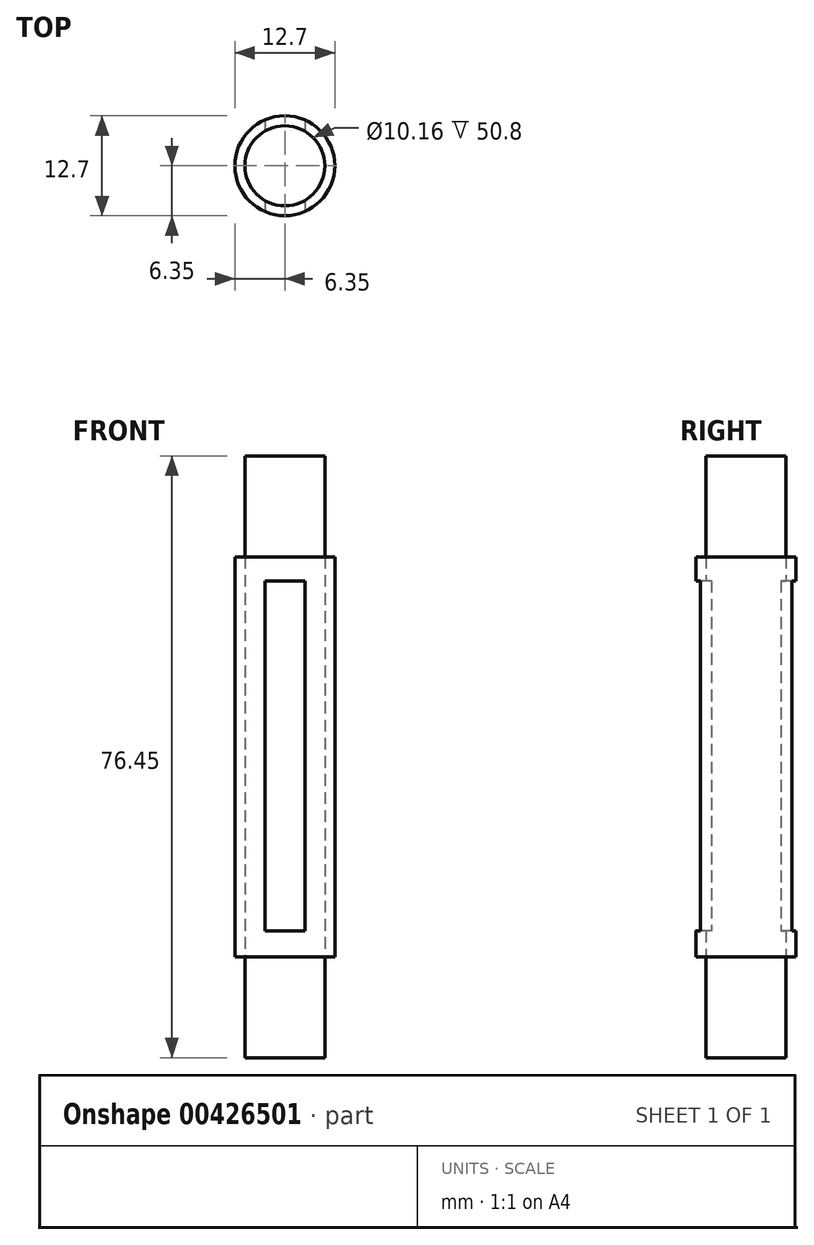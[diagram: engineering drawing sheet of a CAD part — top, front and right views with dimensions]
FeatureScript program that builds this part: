
annotation { "Feature Type Name" : "Feature", "Feature Type Description" : "" }
export const myFeature = defineFeature(function(context is Context, id is Id, definition is map)
    precondition{}
    {
        {
            var Q0;
            Q0=qCreatedBy(makeId("Top.planeOp"),FACE);
            var sketch = newSketch(context, id + "F0", { "sketchPlane" : qUnion([Q0])});
            skCircle(sketch, "E0", {"center": v(0, 0) * mm, "radius": 5.08 * mm});
            skSolve(sketch);
        }
        {
            var Q0;
            Q0=makeQuery(id+"F0.imprint","IMPRINT",FACE,{"disambiguationData":[TD([[makeQuery(id+"F0.imprint","IMPRINT",EDGE,{"derivedFrom":sQuery(id+"F0.wireOp",EDGE,"E0")}),1.0]])]});
            extrude(context, id + "F1", {"entities" : qUnion([Q0]), "depth" : 12.83 * mm});
        }
        {
            var Q0;
            Q0=makeQuery(id+"F1.opExtrude","CAP_FACE",FACE,{"disambiguationData":[OSD([sQuery(id+"F0.wireOp",EDGE,"E0")])],"isStart":false});
            var sketch = newSketch(context, id + "F2", { "sketchPlane" : qUnion([Q0])});
            skCircle(sketch, "E1", {"center": v(0, 0) * mm, "radius": 6.35 * mm});
            skSolve(sketch);
        }
        {
            var Q0;
            Q0=makeQuery(id+"F2.imprint","IMPRINT",FACE,{"disambiguationData":[TD([[makeQuery(id+"F2.imprint","IMPRINT",EDGE,{"derivedFrom":sQuery(id+"F2.wireOp",EDGE,"E1")}),1.0]])]});
            extrude(context, id + "F3", {"entities" : qUnion([Q0]), "depth" : 50.8 * mm});
        }
        {
            var Q0;
            Q0=makeQuery(id+"F3.opExtrude","CAP_FACE",FACE,{"disambiguationData":[OSD([sQuery(id+"F0.wireOp",EDGE,"E0"),sQuery(id+"F2.wireOp",EDGE,"E1")])],"isStart":false});
            var sketch = newSketch(context, id + "F4", { "sketchPlane" : qUnion([Q0])});
            skCircle(sketch, "E2", {"center": v(0, 0) * mm, "radius": 5.08 * mm});
            skSolve(sketch);
        }
        {
            var Q0;
            Q0=makeQuery(id+"F4.imprint","IMPRINT",FACE,{"disambiguationData":[TD([[makeQuery(id+"F4.imprint","IMPRINT",EDGE,{"derivedFrom":sQuery(id+"F4.wireOp",EDGE,"E2")}),1.0]])]});
            extrude(context, id + "F5", {"entities" : qUnion([Q0]), "depth" : 12.83 * mm});
        }
        {
            var Q0;
            Q0=qCreatedBy(makeId("Front.planeOp"),FACE);
            cPlane(context, id + "F6", {"entities" : qUnion([Q0]), "cplaneType" : CPlaneType.OFFSET, "offset" : 6.35 * mm, "width" : 152.4 * mm, "height" : 152.4 * mm});
        }
        {
            var Q0;
            Q0=qCreatedBy(id+"F6.planeOp",FACE);
            var sketch = newSketch(context, id + "F7", { "sketchPlane" : qUnion([Q0])});
            skLineSegment(sketch, "E3", {"start": v(0, 56.52) * mm, "end": v(0, 20.2) * mm, "construction": true});
            skLineSegment(sketch, "E4.bottom", {"start": v(2.54, 60.58) * mm, "end": v(-2.54, 60.58) * mm});
            skLineSegment(sketch, "E4.top", {"start": v(2.54, 16.13) * mm, "end": v(-2.54, 16.13) * mm});
            skLineSegment(sketch, "E4.left", {"start": v(2.54, 60.58) * mm, "end": v(2.54, 16.13) * mm});
            skLineSegment(sketch, "E4.right", {"start": v(-2.54, 60.58) * mm, "end": v(-2.54, 16.13) * mm});
            skPoint(sketch, "E4.middle", {"position": v(0, 38.35) * mm});
            skSolve(sketch);
        }
        {
            var Q0;
            Q0=makeQuery(id+"F7.imprint","IMPRINT",FACE,{"disambiguationData":[TD([[makeQuery(id+"F7.imprint","IMPRINT",EDGE,{"derivedFrom":sQuery(id+"F7.wireOp",EDGE,"E4.bottom")}),1.0]])]});
            extrude(context, id + "F8", {"entities" : qUnion([Q0]), "operationType" : NewBodyOperationType.REMOVE, "oppositeDirection" : true, "depth" : 25.4 * mm});
        }
    });
